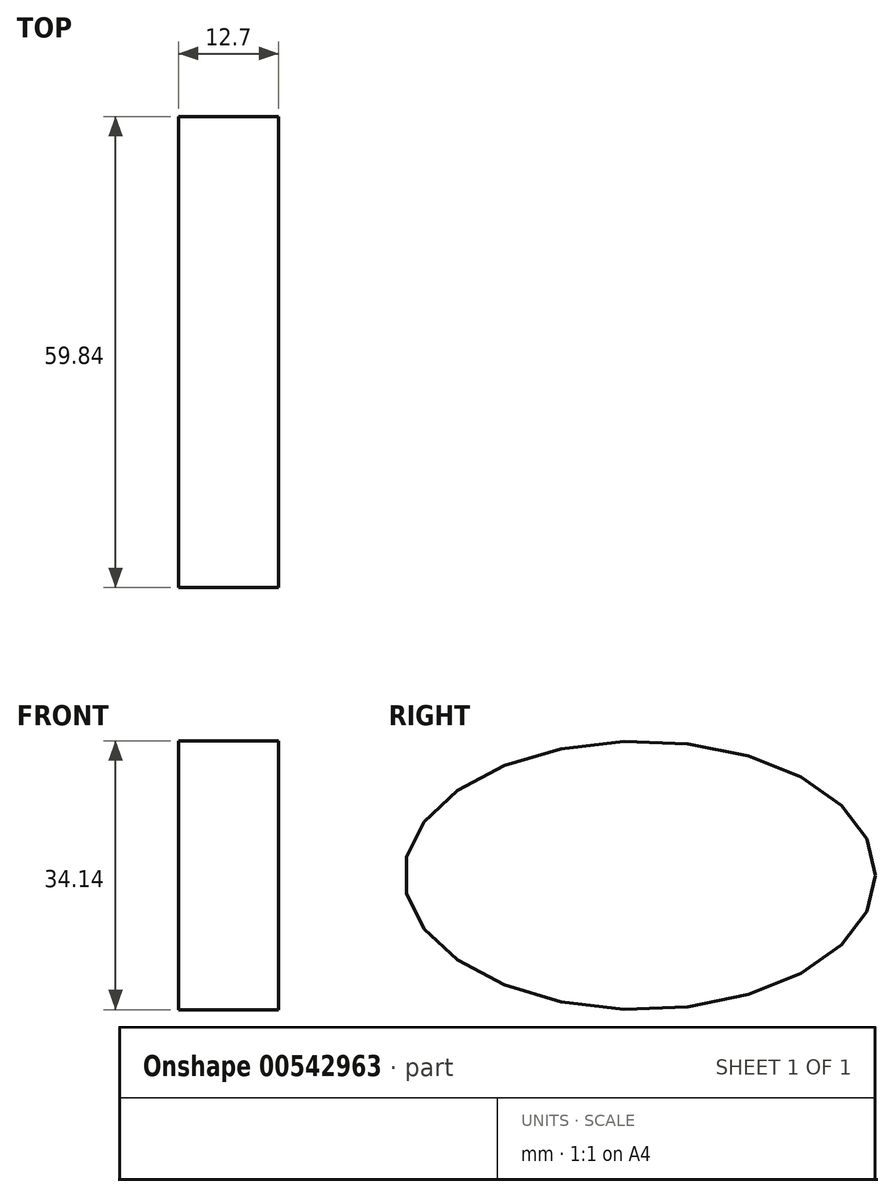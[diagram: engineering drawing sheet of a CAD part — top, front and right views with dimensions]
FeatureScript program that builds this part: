
annotation { "Feature Type Name" : "Feature", "Feature Type Description" : "" }
export const myFeature = defineFeature(function(context is Context, id is Id, definition is map)
    precondition{}
    {
        {
            var Q0;
            Q0=qCreatedBy(makeId("Right.planeOp"),FACE);
            var sketch = newSketch(context, id + "F0", { "sketchPlane" : qUnion([Q0])});
            skEllipse(sketch, "E0", {"center": v(0, 0) * mm, "majorRadius": 29.92 * mm, "minorRadius": 17.07 * mm, "majorAxis": v(1, 0)});
            skSolve(sketch);
        }
        {
            var Q0;
            Q0 = qSketchRegion(id + "F0", true);
            extrude(context, id + "F1", {"entities" : qUnion([Q0]), "depth" : 12.7 * mm, "offsetDistance" : 25.4 * mm});
        }
    });
